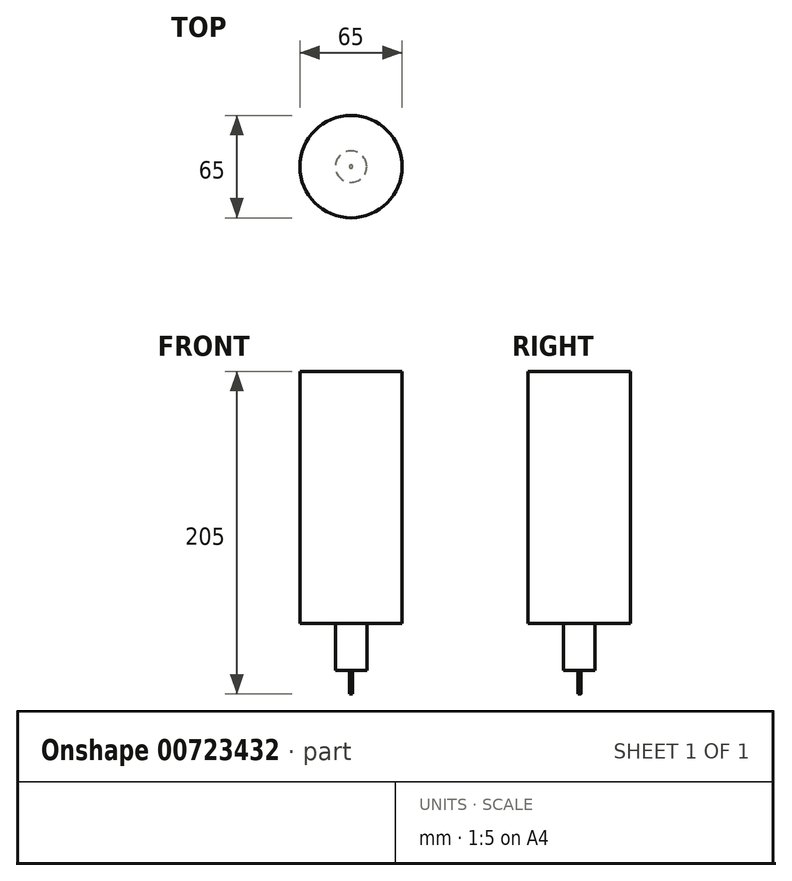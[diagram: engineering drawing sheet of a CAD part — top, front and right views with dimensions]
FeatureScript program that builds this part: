
annotation { "Feature Type Name" : "Feature", "Feature Type Description" : "" }
export const myFeature = defineFeature(function(context is Context, id is Id, definition is map)
    precondition{}
    {
        {
            var Q0;
            Q0=qCreatedBy(makeId("Front.planeOp"),FACE);
            var sketch = newSketch(context, id + "F0", { "sketchPlane" : qUnion([Q0])});
            skLineSegment(sketch, "E0", {"start": v(-32.5, -5.55) * mm, "end": v(-32.5, 154.45) * mm});
            skLineSegment(sketch, "E1", {"start": v(0, 169.07) * mm, "end": v(0, -139.27) * mm, "construction": true});
            skLineSegment(sketch, "E2", {"start": v(-32.5, 154.45) * mm, "end": v(0, 154.45) * mm});
            skLineSegment(sketch, "E3", {"start": v(-10, -5.55) * mm, "end": v(-10, -35.55) * mm});
            skLineSegment(sketch, "E4", {"start": v(-10, -35.55) * mm, "end": v(-1, -35.55) * mm});
            skLineSegment(sketch, "E5", {"start": v(-10, -5.55) * mm, "end": v(-32.5, -5.55) * mm});
            skLineSegment(sketch, "E6", {"start": v(0, 154.45) * mm, "end": v(0, -50.55) * mm});
            skLineSegment(sketch, "E7", {"start": v(-1, -35.55) * mm, "end": v(-1, -50.55) * mm});
            skLineSegment(sketch, "E8", {"start": v(-1, -50.55) * mm, "end": v(0, -50.55) * mm});
            skSolve(sketch);
        }
        {
            var Q0;
            Q0=makeQuery(id+"F0.imprint","IMPRINT",FACE,{"disambiguationData":[TD([[makeQuery(id+"F0.imprint","IMPRINT",EDGE,{"derivedFrom":sQuery(id+"F0.wireOp",EDGE,"E0")}),-1.0]])]});
            var Q1;
            Q1=sQuery(id+"F0.wireOp",EDGE,"E1");
            revolve(context, id + "F1", {"entities" : qUnion([Q0]), "axis" : qUnion([Q1]), "revolveType" : RevolveType.FULL});
        }
    });
